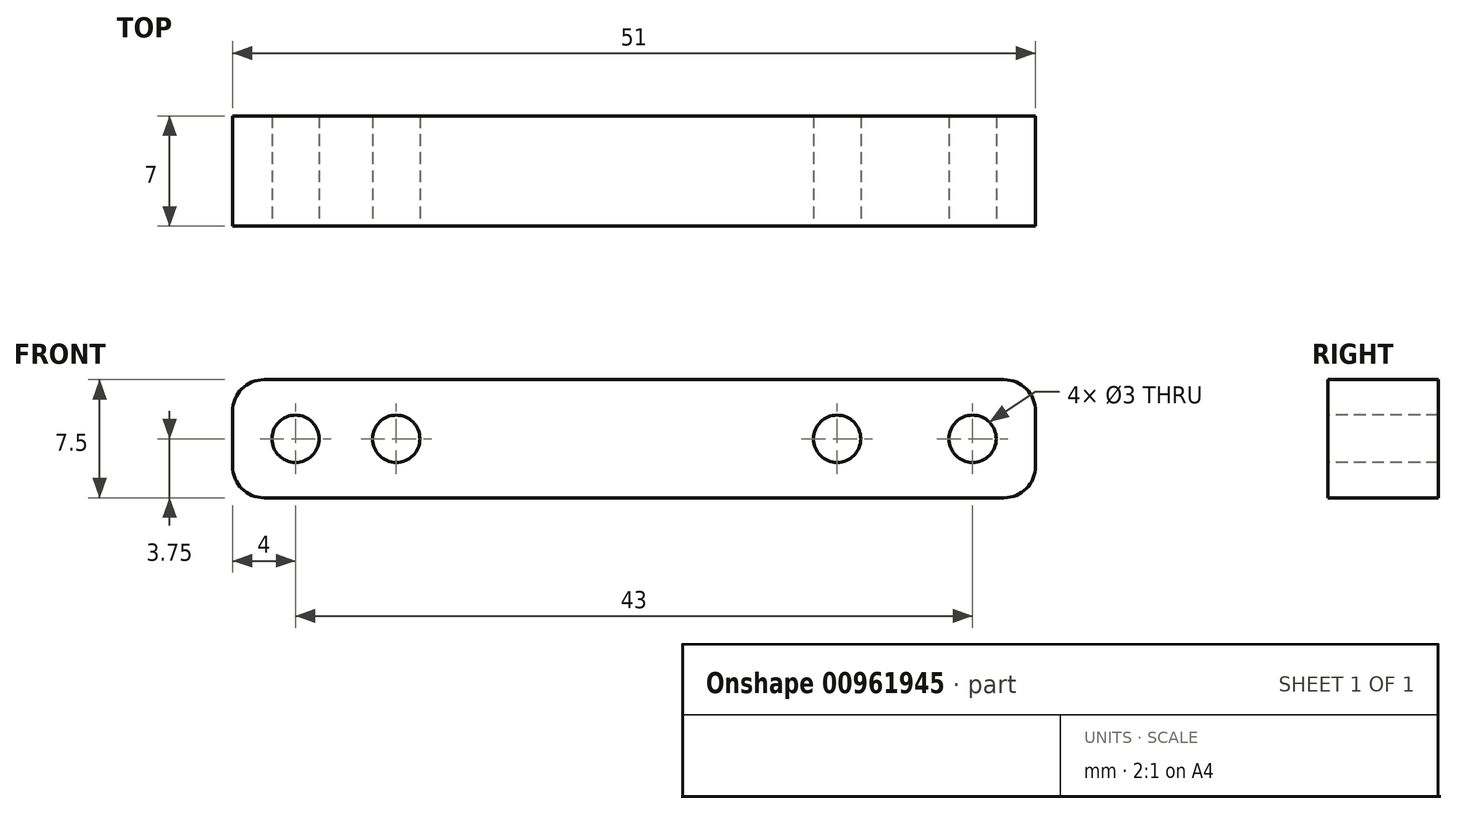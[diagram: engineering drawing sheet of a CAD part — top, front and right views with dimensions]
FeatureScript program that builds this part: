
annotation { "Feature Type Name" : "Feature", "Feature Type Description" : "" }
export const myFeature = defineFeature(function(context is Context, id is Id, definition is map)
    precondition{}
    {
        {
            var Q0;
            Q0=qCreatedBy(makeId("Top.planeOp"),FACE);
            var sketch = newSketch(context, id + "F0", { "sketchPlane" : qUnion([Q0])});
            skLineSegment(sketch, "E0.bottom", {"start": v(25.5, -3.5) * mm, "end": v(-25.5, -3.5) * mm});
            skLineSegment(sketch, "E0.top", {"start": v(25.5, 3.5) * mm, "end": v(-25.5, 3.5) * mm});
            skLineSegment(sketch, "E0.left", {"start": v(25.5, -3.5) * mm, "end": v(25.5, 3.5) * mm});
            skLineSegment(sketch, "E0.right", {"start": v(-25.5, -3.5) * mm, "end": v(-25.5, 3.5) * mm});
            skPoint(sketch, "E0.middle", {"position": v(0, 0) * mm});
            skSolve(sketch);
        }
        {
            var Q0;
            Q0=makeQuery(id+"F0.imprint","IMPRINT",FACE,{"disambiguationData":[TD([[makeQuery(id+"F0.imprint","IMPRINT",EDGE,{"derivedFrom":sQuery(id+"F0.wireOp",EDGE,"E0.bottom")}),-1.0]])]});
            extrude(context, id + "F1", {"entities" : qUnion([Q0]), "flatOperationType" : FlatOperationType.REMOVE, "depth" : 7.5 * mm, "offsetDistance" : 25 * mm, "domain" : OperationDomain.MODEL, "symmetric" : true});
        }
        {
            var Q0;
            Q0=makeQuery(id+"F1.opExtrude","CAP_EDGE",EDGE,{"disambiguationData":[OSD([sQuery(id+"F0.wireOp",EDGE,"E0.right")])],"isStart":false});
            fillet(context, id + "F2", {"entities" : qUnion([Q0]), "radius" : 2 * mm, "tangentPropagation" : true, "allowEdgeOverflow" : false});
        }
        {
            var Q0;
            Q0=makeQuery(id+"F1.opExtrude","CAP_EDGE",EDGE,{"disambiguationData":[OSD([sQuery(id+"F0.wireOp",EDGE,"E0.right")])],"isStart":true});
            fillet(context, id + "F3", {"entities" : qUnion([Q0]), "radius" : 2 * mm, "tangentPropagation" : true, "allowEdgeOverflow" : false});
        }
        {
            var Q0;
            Q0=makeQuery(id+"F1.opExtrude","CAP_EDGE",EDGE,{"disambiguationData":[OSD([sQuery(id+"F0.wireOp",EDGE,"E0.left")])],"isStart":false});
            fillet(context, id + "F4", {"entities" : qUnion([Q0]), "radius" : 2 * mm, "tangentPropagation" : true, "allowEdgeOverflow" : false});
        }
        {
            var Q0;
            Q0=makeQuery(id+"F1.opExtrude","CAP_EDGE",EDGE,{"disambiguationData":[OSD([sQuery(id+"F0.wireOp",EDGE,"E0.left")])],"isStart":true});
            fillet(context, id + "F5", {"entities" : qUnion([Q0]), "radius" : 2 * mm, "tangentPropagation" : true, "allowEdgeOverflow" : false});
        }
        {
            var Q0;
            Q0=qCreatedBy(makeId("Front.planeOp"),FACE);
            var sketch = newSketch(context, id + "F6", { "sketchPlane" : qUnion([Q0])});
            skLineSegment(sketch, "E1.0.0", {"start": v(-23.5, -3.75) * mm, "end": v(23.5, -3.75) * mm});
            skArc(sketch, "E1.0.1", {"start": v(23.5, -3.75) * mm, "mid": v(24.91, -3.16) * mm, "end": v(25.5, -1.75) * mm});
            skLineSegment(sketch, "E1.0.2", {"start": v(25.5, -1.75) * mm, "end": v(25.5, 1.75) * mm});
            skArc(sketch, "E1.0.3", {"start": v(25.5, 1.75) * mm, "mid": v(24.91, 3.16) * mm, "end": v(23.5, 3.75) * mm});
            skLineSegment(sketch, "E1.0.4", {"start": v(23.5, 3.75) * mm, "end": v(-23.5, 3.75) * mm});
            skArc(sketch, "E1.0.5", {"start": v(-23.5, 3.75) * mm, "mid": v(-24.91, 3.16) * mm, "end": v(-25.5, 1.75) * mm});
            skLineSegment(sketch, "E1.0.6", {"start": v(-25.5, 1.75) * mm, "end": v(-25.5, -1.75) * mm});
            skArc(sketch, "E1.0.7", {"start": v(-25.5, -1.75) * mm, "mid": v(-24.91, -3.16) * mm, "end": v(-23.5, -3.75) * mm});
            skCircle(sketch, "E2", {"center": v(-21.5, 0) * mm, "radius": 1.5 * mm});
            skCircle(sketch, "E3", {"center": v(21.5, 0) * mm, "radius": 1.5 * mm});
            skSolve(sketch);
        }
        {
            var Q0;
            Q0 = qSketchRegion(id + "F6", true);
            extrude(context, id + "F7", {"entities" : qUnion([Q0]), "operationType" : NewBodyOperationType.INTERSECT, "oppositeDirection" : true, "depth" : 7 * mm, "offsetDistance" : 25 * mm, "symmetric" : true});
        }
        {
            var Q0;
            Q0=qCreatedBy(makeId("Front.planeOp"),FACE);
            var sketch = newSketch(context, id + "F8", { "sketchPlane" : qUnion([Q0])});
            skCircle(sketch, "E4", {"center": v(-15.1, 0) * mm, "radius": 1.5 * mm});
            skCircle(sketch, "E5", {"center": v(12.9, 0) * mm, "radius": 1.5 * mm});
            skSolve(sketch);
        }
        {
            var Q0;
            Q0 = qSketchRegion(id + "F8", true);
            extrude(context, id + "F9", {"entities" : qUnion([Q0]), "operationType" : NewBodyOperationType.REMOVE, "oppositeDirection" : true, "depth" : 7 * mm, "offsetDistance" : 25 * mm, "symmetric" : true});
        }
    });
